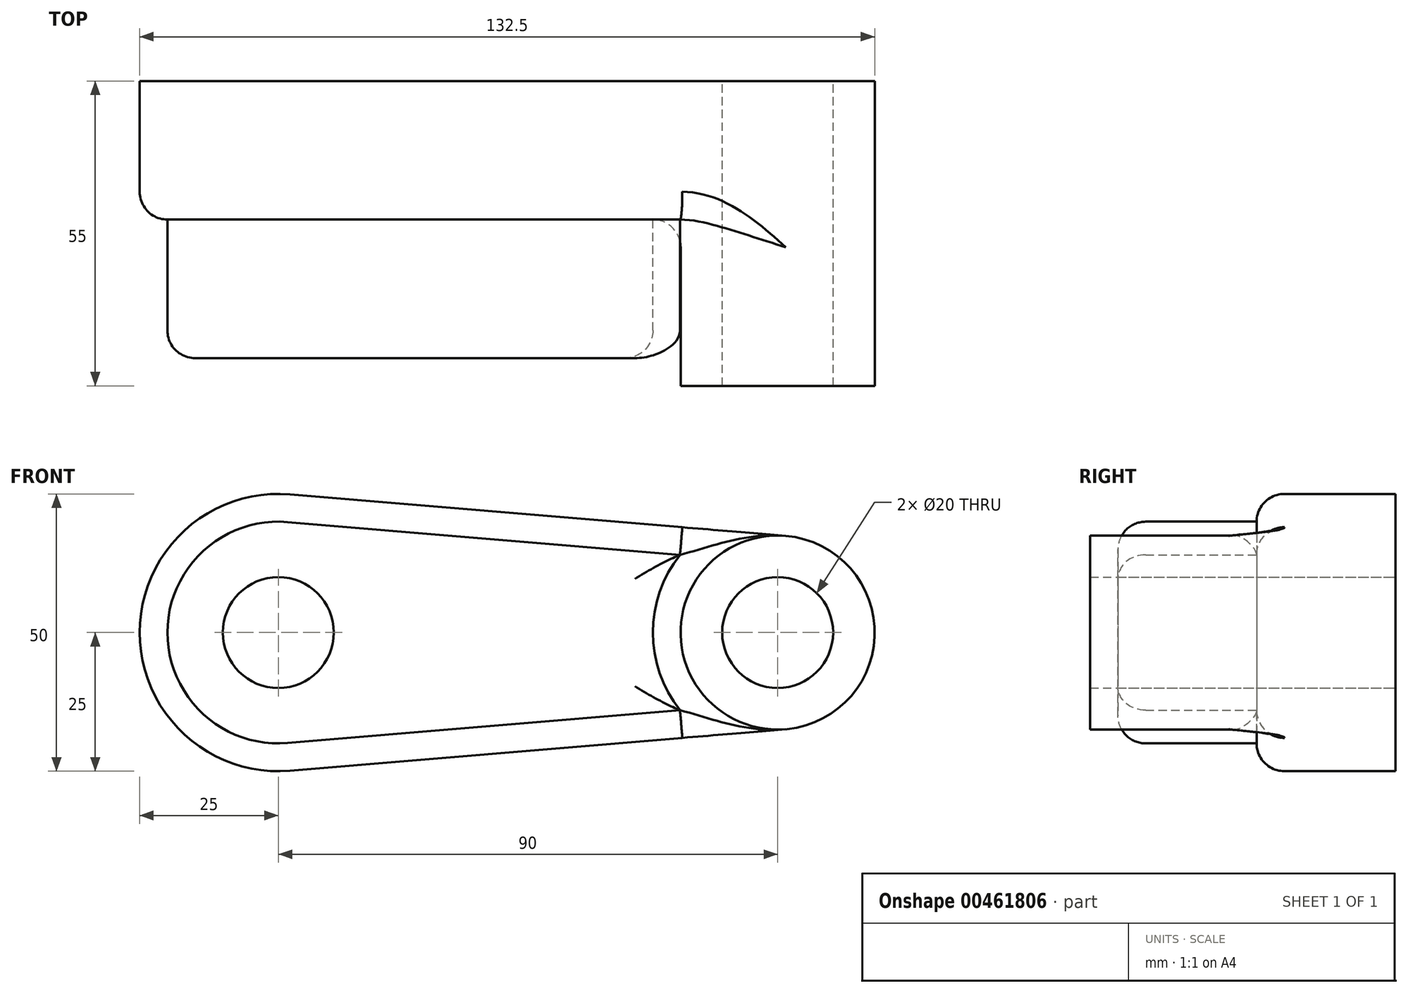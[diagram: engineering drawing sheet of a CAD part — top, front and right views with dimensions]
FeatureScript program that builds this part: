
annotation { "Feature Type Name" : "Feature", "Feature Type Description" : "" }
export const myFeature = defineFeature(function(context is Context, id is Id, definition is map)
    precondition{}
    {
        {
            var Q0;
            Q0=qCreatedBy(makeId("Front.planeOp"),FACE);
            var sketch = newSketch(context, id + "F0", { "sketchPlane" : qUnion([Q0])});
            skCircle(sketch, "E0", {"center": v(0, 0) * mm, "radius": 25 * mm});
            skCircle(sketch, "E1", {"center": v(90, 0) * mm, "radius": 17.5 * mm});
            skLineSegment(sketch, "E2", {"start": v(2.08, 24.91) * mm, "end": v(91.46, 17.44) * mm});
            skLineSegment(sketch, "E3", {"start": v(2.08, -24.91) * mm, "end": v(91.46, -17.44) * mm});
            skCircle(sketch, "E4", {"center": v(0, 0) * mm, "radius": 10 * mm});
            skCircle(sketch, "E5", {"center": v(90, 0) * mm, "radius": 10 * mm});
            skSolve(sketch);
        }
        {
            var Q0;
            Q0=qSketchRegion(id+"F0",true);
            extrude(context, id + "F1", {"entities" : qUnion([Q0]), "depth" : 25 * mm});
        }
        {
            var Q0;
            Q0=makeQuery(id+"F0.imprint","IMPRINT",FACE,{"disambiguationData":[TD([[makeQuery(id+"F0.imprint","IMPRINT",EDGE,{"derivedFrom":sQuery(id+"F0.wireOp",EDGE,"E5")}),-1.0]])]});
            extrude(context, id + "F2", {"entities" : qUnion([Q0]), "operationType" : NewBodyOperationType.ADD, "depth" : 55 * mm, "offsetDistance" : 25 * mm});
        }
        {
            var Q0;
            {var subQ0=sQuery(id+"F0.wireOp",EDGE,"E1");Q0=makeQuery(id+"F2.boolean.opBoolean","INTERSECT",EDGE,{"derivedFrom":[makeQuery(id+"F1.opExtrude","CAP_FACE",FACE,{"disambiguationData":[OSD([sQuery(id+"F0.wireOp",EDGE,"E0"),subQ0,sQuery(id+"F0.wireOp",EDGE,"E2"),sQuery(id+"F0.wireOp",EDGE,"E3"),sQuery(id+"F0.wireOp",EDGE,"E4"),sQuery(id+"F0.wireOp",EDGE,"E5")])],"isStart":false}),makeQuery(id+"F2.opExtrude","SWEPT_FACE",FACE,{"disambiguationData":[OSD([subQ0])]})]});}
            fillet(context, id + "F3", {"entities" : qUnion([Q0]), "radius" : 5 * mm, "tangentPropagation" : true, "allowEdgeOverflow" : false});
        }
        {
            var Q0;
            Q0=makeQuery(id+"F1.opExtrude","CAP_EDGE",EDGE,{"disambiguationData":[OSD([sQuery(id+"F0.wireOp",EDGE,"E2")])],"isStart":false});
            fillet(context, id + "F4", {"entities" : qUnion([Q0]), "radius" : 5 * mm, "tangentPropagation" : true, "allowEdgeOverflow" : false});
        }
        {
            var Q0;
            Q0=makeQuery(id+"F1.opExtrude","CAP_FACE",FACE,{"disambiguationData":[OSD([sQuery(id+"F0.wireOp",EDGE,"E0"),sQuery(id+"F0.wireOp",EDGE,"E1"),sQuery(id+"F0.wireOp",EDGE,"E2"),sQuery(id+"F0.wireOp",EDGE,"E3"),sQuery(id+"F0.wireOp",EDGE,"E4"),sQuery(id+"F0.wireOp",EDGE,"E5")])],"isStart":false});
            extrude(context, id + "F5", {"entities" : qUnion([Q0]), "operationType" : NewBodyOperationType.ADD, "depth" : 25 * mm, "offsetDistance" : 25 * mm});
        }
        {
            var Q0;
            {var subQ0=sQuery(id+"F0.wireOp",EDGE,"E5");var subQ1=sQuery(id+"F0.wireOp",EDGE,"E4");var subQ2=sQuery(id+"F0.wireOp",EDGE,"E3");var subQ3=sQuery(id+"F0.wireOp",EDGE,"E2");var subQ4=sQuery(id+"F0.wireOp",EDGE,"E1");var subQ5=sQuery(id+"F0.wireOp",EDGE,"E0");var subQ6=makeQuery(id+"F1.opExtrude","CAP_FACE",FACE,{"disambiguationData":[OSD([subQ5,subQ4,subQ3,subQ2,subQ1,subQ0])],"isStart":false});Q0=makeQuery(id+"F5.opExtrude","CAP_EDGE",EDGE,{"disambiguationData":[OSD([subQ5,subQ4,subQ3,subQ2,subQ1,subQ0]),TDD([makeQuery(id+"F3.opFillet","BLEND_EDGE",EDGE,{"blendedFrom":[makeQuery(id+"F2.boolean.opBoolean","INTERSECT",EDGE,{"derivedFrom":[subQ6,makeQuery(id+"F2.opExtrude","SWEPT_FACE",FACE,{"disambiguationData":[OSD([subQ4])]})]}),subQ6],"blendedInto":[subQ6]})])],"isStart":false});}
            var Q1;
            {var subQ0=sQuery(id+"F0.wireOp",EDGE,"E5");var subQ1=sQuery(id+"F0.wireOp",EDGE,"E4");var subQ2=sQuery(id+"F0.wireOp",EDGE,"E3");var subQ3=sQuery(id+"F0.wireOp",EDGE,"E2");var subQ4=sQuery(id+"F0.wireOp",EDGE,"E1");var subQ5=sQuery(id+"F0.wireOp",EDGE,"E0");Q1=makeQuery(id+"F5.opExtrude","CAP_EDGE",EDGE,{"disambiguationData":[OSD([subQ5,subQ4,subQ3,subQ2,subQ1,subQ0]),TDD([makeQuery(id+"F4.opFillet","BLEND_EDGE",EDGE,{"blendedFrom":[makeQuery(id+"F1.opExtrude","CAP_EDGE",EDGE,{"disambiguationData":[OSD([subQ3])],"isStart":false}),makeQuery(id+"F1.opExtrude","CAP_FACE",FACE,{"disambiguationData":[OSD([subQ5,subQ4,subQ3,subQ2,subQ1,subQ0])],"isStart":false})],"blendedInto":[makeQuery(id+"F1.opExtrude","CAP_FACE",FACE,{"disambiguationData":[OSD([subQ5,subQ4,subQ3,subQ2,subQ1,subQ0])],"isStart":false})]})])],"isStart":false});}
            fillet(context, id + "F6", {"entities" : qUnion([Q0, Q1]), "radius" : 5 * mm, "tangentPropagation" : true, "allowEdgeOverflow" : false});
        }
    });
